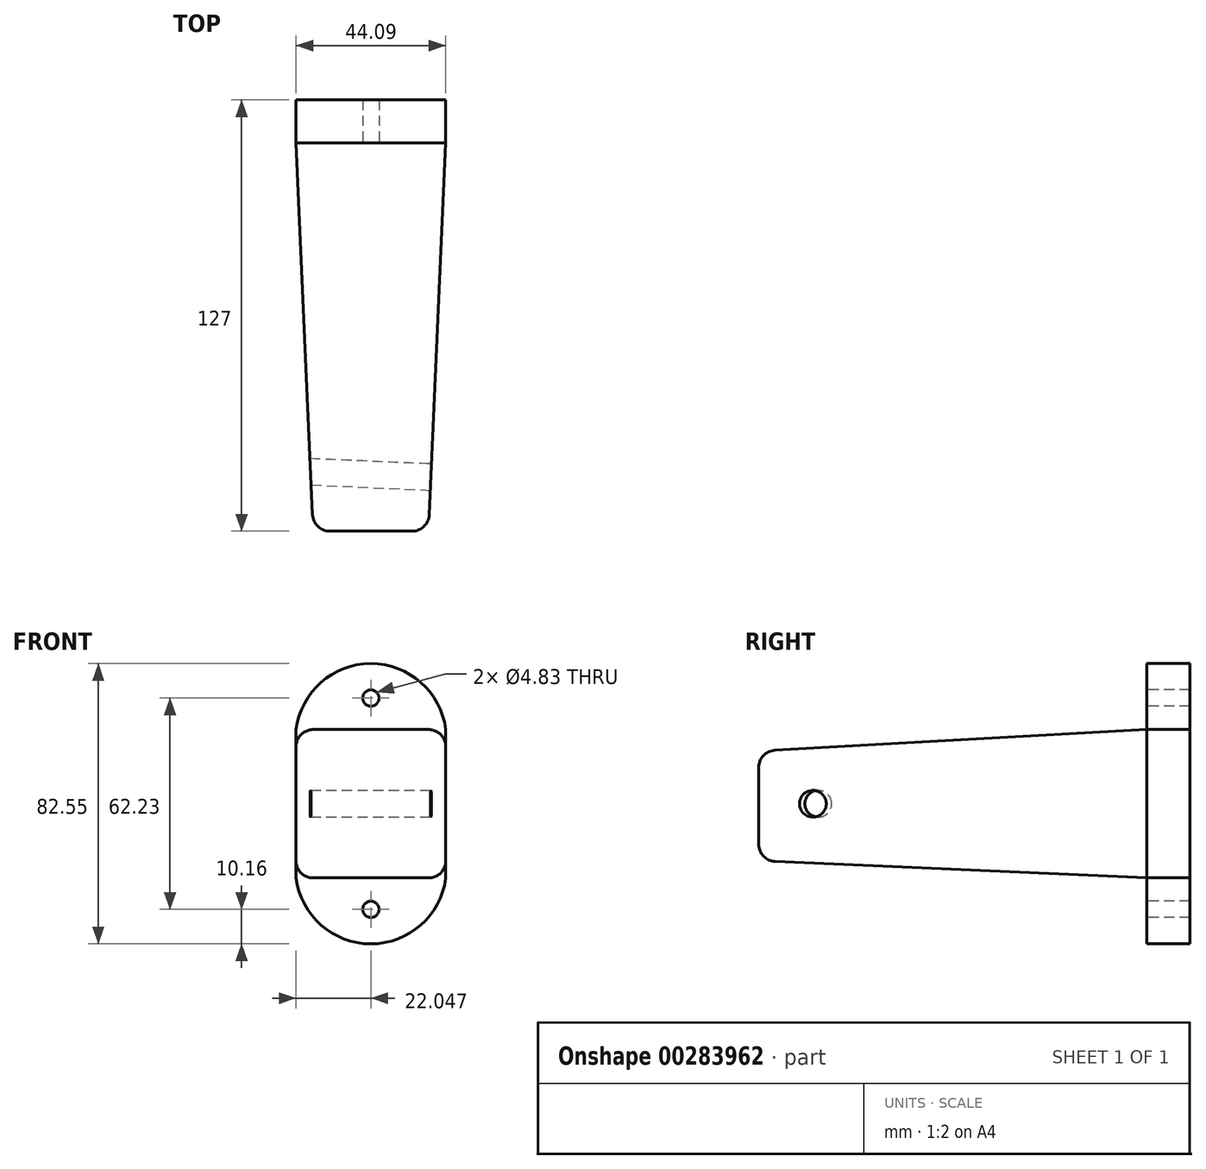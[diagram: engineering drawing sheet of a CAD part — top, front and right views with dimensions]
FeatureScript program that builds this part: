
annotation { "Feature Type Name" : "Feature", "Feature Type Description" : "" }
export const myFeature = defineFeature(function(context is Context, id is Id, definition is map)
    precondition{}
    {
        {
            var Q0;
            Q0=qCreatedBy(makeId("Front.planeOp"),FACE);
            var sketch = newSketch(context, id + "F0", { "sketchPlane" : qUnion([Q0])});
            skLineSegment(sketch, "E0", {"start": v(0, 19.42) * mm, "end": v(0, 63.13) * mm});
            skArc(sketch, "E1", {"start": v(44.1, 63.13) * mm, "mid": v(22.05, 82.55) * mm, "end": v(0, 63.13) * mm});
            skArc(sketch, "E2", {"start": v(0, 19.42) * mm, "mid": v(22.05, 0) * mm, "end": v(44.1, 19.42) * mm});
            skPoint(sketch, "E3.orphan", {"position": v(44.1, 82.55) * mm});
            skPoint(sketch, "E4.orphan", {"position": v(0, 82.55) * mm});
            skPoint(sketch, "E5.orphan", {"position": v(0, 0) * mm});
            skPoint(sketch, "E6.end.orphan", {"position": v(44.1, 0) * mm});
            skLineSegment(sketch, "E7", {"start": v(44.1, 19.42) * mm, "end": v(44.1, 63.13) * mm});
            skLineSegment(sketch, "E8", {"start": v(0, 0) * mm, "end": v(0, 19.42) * mm});
            skSolve(sketch);
        }
        {
            var Q0;
            Q0 = qSketchRegion(id + "F0", true);
            extrude(context, id + "F1", {"entities" : qUnion([Q0]), "depth" : 12.7 * mm});
        }
        {
            var Q0;
            Q0=makeQuery(id+"F1.opExtrude","CAP_FACE",FACE,{"disambiguationData":[OSD([sQuery(id+"F0.wireOp",EDGE,"E0"),sQuery(id+"F0.wireOp",EDGE,"E1"),sQuery(id+"F0.wireOp",EDGE,"E2"),sQuery(id+"F0.wireOp",EDGE,"E7")])],"isStart":false});
            var sketch = newSketch(context, id + "F2", { "sketchPlane" : qUnion([Q0])});
            skLineSegment(sketch, "E9", {"start": v(0, 63.13) * mm, "end": v(44.1, 63.13) * mm});
            skLineSegment(sketch, "E10", {"start": v(0, 19.42) * mm, "end": v(44.1, 19.42) * mm});
            skLineSegment(sketch, "E11", {"start": v(44.1, 19.42) * mm, "end": v(44.1, 63.13) * mm});
            skLineSegment(sketch, "E12", {"start": v(0, 19.42) * mm, "end": v(0, 63.13) * mm});
            skSolve(sketch);
        }
        {
            var Q0;
            Q0=qCreatedBy(makeId("Front.planeOp"),FACE);
            cPlane(context, id + "F3", {"entities" : qUnion([Q0]), "cplaneType" : CPlaneType.OFFSET, "offset" : 127 * mm, "width" : 152.4 * mm, "height" : 152.4 * mm});
        }
        {
            var Q0;
            Q0=qCreatedBy(id+"F3.planeOp",FACE);
            var sketch = newSketch(context, id + "F4", { "sketchPlane" : qUnion([Q0])});
            skLineSegment(sketch, "E13.0", {"start": v(5.08, 24.5) * mm, "end": v(39.01, 24.5) * mm});
            skLineSegment(sketch, "E14.0", {"start": v(5.08, 24.5) * mm, "end": v(5.08, 56.74) * mm});
            skLineSegment(sketch, "E15.MirrorCS", {"start": v(39.01, 24.5) * mm, "end": v(39.01, 56.74) * mm});
            skPoint(sketch, "E16.orphan", {"position": v(5.08, 19.43) * mm});
            skPoint(sketch, "E17.orphan", {"position": v(0, 24.5) * mm});
            skPoint(sketch, "E18.orphan", {"position": v(44.1, 24.5) * mm});
            skPoint(sketch, "E19.orphan", {"position": v(39.01, 19.43) * mm});
            skLineSegment(sketch, "E20.MirrorCS", {"start": v(5.08, 56.74) * mm, "end": v(39.01, 56.74) * mm});
            skPoint(sketch, "E21.orphan", {"position": v(5.08, 62.7) * mm});
            skPoint(sketch, "E22.orphan", {"position": v(39.01, 62.7) * mm});
            skPoint(sketch, "E23.start.orphan", {"position": v(22.05, 24.5) * mm});
            skSolve(sketch);
        }
        {
            var Q1;
            Q1=makeQuery(id+"F2.imprint","IMPRINT",FACE,{"disambiguationData":[TD([[makeQuery(id+"F2.imprint","IMPRINT",EDGE,{"derivedFrom":sQuery(id+"F2.wireOp",EDGE,"E9")}),-1.0]])]});
            var Q2;
            Q2=makeQuery(id+"F4.imprint","IMPRINT",FACE,{"disambiguationData":[TD([[makeQuery(id+"F4.imprint","IMPRINT",EDGE,{"derivedFrom":sQuery(id+"F4.wireOp",EDGE,"E13.0")}),1.0]])]});
            loft(context, id + "F5", {"operationType" : NewBodyOperationType.ADD, "sheetProfilesArray" : [{ "sheetProfileEntities" : qUnion([Q1]) }, { "sheetProfileEntities" : qUnion([Q2]) }]});
        }
        {
            var Q0;
            Q0=makeQuery(id+"F5.opLoft","SWEPT_EDGE",EDGE,{"disambiguationData":[OSD([sQuery(id+"F0.wireOp",EDGE,"E2"),sQuery(id+"F2.wireOp",EDGE,"E10"),sQuery(id+"F2.wireOp",EDGE,"E11"),sQuery(id+"F4.wireOp",EDGE,"E13.0"),sQuery(id+"F4.wireOp",EDGE,"E15.MirrorCS")])]});
            var Q1;
            Q1=makeQuery(id+"F5.opLoft","MID_CAP_EDGE",EDGE,{"disambiguationData":[OSD([sQuery(id+"F4.wireOp",EDGE,"E13.0"),sQuery(id+"F4.wireOp",EDGE,"E15.MirrorCS"),sQuery(id+"F4.wireOp",EDGE,"E20.MirrorCS")])],"capPos":1.0});
            var Q2;
            Q2=makeQuery(id+"F5.opLoft","MID_CAP_EDGE",EDGE,{"disambiguationData":[OSD([sQuery(id+"F4.wireOp",EDGE,"E14.0"),sQuery(id+"F4.wireOp",EDGE,"E15.MirrorCS"),sQuery(id+"F4.wireOp",EDGE,"E20.MirrorCS")])],"capPos":1.0});
            var Q3;
            Q3=makeQuery(id+"F5.opLoft","SWEPT_EDGE",EDGE,{"disambiguationData":[OSD([sQuery(id+"F0.wireOp",EDGE,"E1"),sQuery(id+"F2.wireOp",EDGE,"E9"),sQuery(id+"F2.wireOp",EDGE,"E11"),sQuery(id+"F4.wireOp",EDGE,"E15.MirrorCS"),sQuery(id+"F4.wireOp",EDGE,"E20.MirrorCS")])]});
            var Q4;
            Q4=makeQuery(id+"F5.opLoft","MID_CAP_EDGE",EDGE,{"disambiguationData":[OSD([sQuery(id+"F4.wireOp",EDGE,"E13.0"),sQuery(id+"F4.wireOp",EDGE,"E14.0"),sQuery(id+"F4.wireOp",EDGE,"E15.MirrorCS")])],"capPos":1.0});
            var Q5;
            Q5=makeQuery(id+"F5.opLoft","MID_CAP_EDGE",EDGE,{"disambiguationData":[OSD([sQuery(id+"F4.wireOp",EDGE,"E13.0"),sQuery(id+"F4.wireOp",EDGE,"E14.0"),sQuery(id+"F4.wireOp",EDGE,"E20.MirrorCS")])],"capPos":1.0});
            var Q6;
            Q6=makeQuery(id+"F5.opLoft","SWEPT_EDGE",EDGE,{"disambiguationData":[OSD([sQuery(id+"F0.wireOp",EDGE,"E2"),sQuery(id+"F2.wireOp",EDGE,"E10"),sQuery(id+"F2.wireOp",EDGE,"E12"),sQuery(id+"F4.wireOp",EDGE,"E13.0"),sQuery(id+"F4.wireOp",EDGE,"E14.0")])]});
            var Q7;
            Q7=makeQuery(id+"F5.opLoft","SWEPT_EDGE",EDGE,{"disambiguationData":[OSD([sQuery(id+"F0.wireOp",EDGE,"E1"),sQuery(id+"F2.wireOp",EDGE,"E9"),sQuery(id+"F2.wireOp",EDGE,"E12"),sQuery(id+"F4.wireOp",EDGE,"E14.0"),sQuery(id+"F4.wireOp",EDGE,"E20.MirrorCS")])]});
            fillet(context, id + "F6", {"entities" : qUnion([Q0, Q1, Q2, Q3, Q4, Q5, Q6, Q7]), "radius" : 5.08 * mm, "tangentPropagation" : true, "allowEdgeOverflow" : false});
        }
        {
            var Q0;
            Q0=makeQuery(id+"F5.opLoft","SWEPT_FACE",FACE,{"disambiguationData":[OSD([sQuery(id+"F0.wireOp",EDGE,"E1"),sQuery(id+"F0.wireOp",EDGE,"E2"),sQuery(id+"F2.wireOp",EDGE,"E9"),sQuery(id+"F2.wireOp",EDGE,"E10"),sQuery(id+"F2.wireOp",EDGE,"E11"),sQuery(id+"F4.wireOp",EDGE,"E13.0"),sQuery(id+"F4.wireOp",EDGE,"E15.MirrorCS"),sQuery(id+"F4.wireOp",EDGE,"E20.MirrorCS")])]});
            var sketch = newSketch(context, id + "F7", { "sketchPlane" : qUnion([Q0])});
            skLineSegment(sketch, "E24", {"start": v(-10.73, 24.5) * mm, "end": v(-10.73, 58.06) * mm});
            skLineSegment(sketch, "E25", {"start": v(-10.73, 41.27) * mm, "end": v(-109.15, 41.27) * mm});
            skPoint(sketch, "E25.endSnap0", {"position": v(-10.73, 41.27) * mm});
            skCircle(sketch, "E26", {"center": v(-109.15, 41.27) * mm, "radius": 3.94 * mm});
            skSolve(sketch);
        }
        {
            var Q0;
            Q0=sQuery(id+"F7.wireOp",VERTEX,"E26.center");
            var Q1;
            Q1=makeQuery(id+"F1.opExtrude","SWEPT_BODY",BODY,{"disambiguationData":[OSD([sQuery(id+"F0.wireOp",EDGE,"E0"),sQuery(id+"F0.wireOp",EDGE,"E1"),sQuery(id+"F0.wireOp",EDGE,"E2"),sQuery(id+"F0.wireOp",EDGE,"E7")])]});
            hole(context, id + "F8", {"style" : HoleStyle.SIMPLE, "endStyle" : HoleEndStyle.THROUGH, "holeDiameter" : 7.87 * mm, "tappedDepth" : 12.7 * mm, "tapClearance" : 3, "locations" : qUnion([Q0]), "scope" : qUnion([Q1])});
        }
        {
            var Q0;
            {var subQ6=sQuery(id+"F0.wireOp",EDGE,"E2");var subQ7=sQuery(id+"F0.wireOp",EDGE,"E1");var subQ8=sQuery(id+"F0.wireOp",EDGE,"E7");var subQ11=sQuery(id+"F0.wireOp",EDGE,"E0");Q0=makeQuery(id+"F5.boolean.opBoolean","SPLIT",FACE,{"disambiguationData":[TD([makeQuery(id+"F1.opExtrude","SWEPT_FACE",FACE,{"disambiguationData":[OSD([subQ7])]})])],"derivedFrom":makeQuery(id+"F1.opExtrude","CAP_FACE",FACE,{"disambiguationData":[OSD([subQ11,subQ7,subQ6,subQ8])],"isStart":false})});}
            var sketch = newSketch(context, id + "F9", { "sketchPlane" : qUnion([Q0])});
            skLineSegment(sketch, "E27", {"start": v(22.05, 82.55) * mm, "end": v(22.05, 72.39) * mm});
            skCircle(sketch, "E28", {"center": v(22.05, 72.39) * mm, "radius": 2.41 * mm});
            skCircle(sketch, "E29.MirrorC", {"center": v(22.05, 10.16) * mm, "radius": 2.41 * mm});
            skSolve(sketch);
        }
        {
            var Q0;
            Q0 = qSketchRegion(id + "F9", true);
            extrude(context, id + "F10", {"entities" : qUnion([Q0]), "operationType" : NewBodyOperationType.REMOVE, "oppositeDirection" : true, "depth" : 12.7 * mm});
        }
    });
